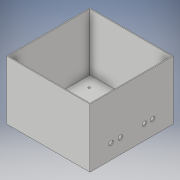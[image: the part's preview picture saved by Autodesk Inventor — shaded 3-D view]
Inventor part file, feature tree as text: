
AUTODESK INVENTOR PART (.ipt)
format: ipt  version: 2018 (Build 220112000, 112)  size: 155,136 bytes
history: native  units: in
note: dims shown in document units (in); Inventor stores cm internally (conversion verified against a paired STEP export)
features: sketch x7, extrude x6
ambient origin geometry x8: Origin, YZ Plane, XZ Plane, XY Plane, X Axis, Y Axis, Z Axis, Center Point
bodies: Solid1 (feature_tree)
feature tree (13):
  extrude  "Extrusion1"  Depth=4.76in
  extrude  "Extrusion2"  Depth=4.66in
  extrude  "Extrusion3"  Depth=3.26in TaperAngle=0.0deg
  extrude  "Extrusion4"  Depth=0.164in
  extrude  "Extrusion5"  Depth=3.937in
  sketch  "Sketch6"  dims[d15=3.937in d21=0.112in]
  extrude  "Extrusion6"  Depth=0.112in
  sketch  "Sketch1"  dims[d0=4.76in d1=4.76in]
  sketch  "Sketch2"  dims[d2=0.1in d3=0.0in d4=4.66in]
  sketch  "Sketch3"  dims[d5=4.66in d6=3.26in d7=0.0in]
  sketch  "Sketch4"  dims[d10=0.164in d11=0.164in]
  sketch  "Sketch5"  dims[d12=0.0in d13=0.0in d14=3.937in]
  sketch  "Sketch7"  dims[d22=0.112in d23=0.112in d24=2.598in d25=0.787in d26=0.118in d27=0.118in d28=0.118in d29=0.118in d30=0.0in d31=0.0in d35=0.25in d36=1.0in d37=0.0in d44=0.25in d45=0.25in d46=0.25in d47=0.25in d48=0.0in d49=0.0in]
